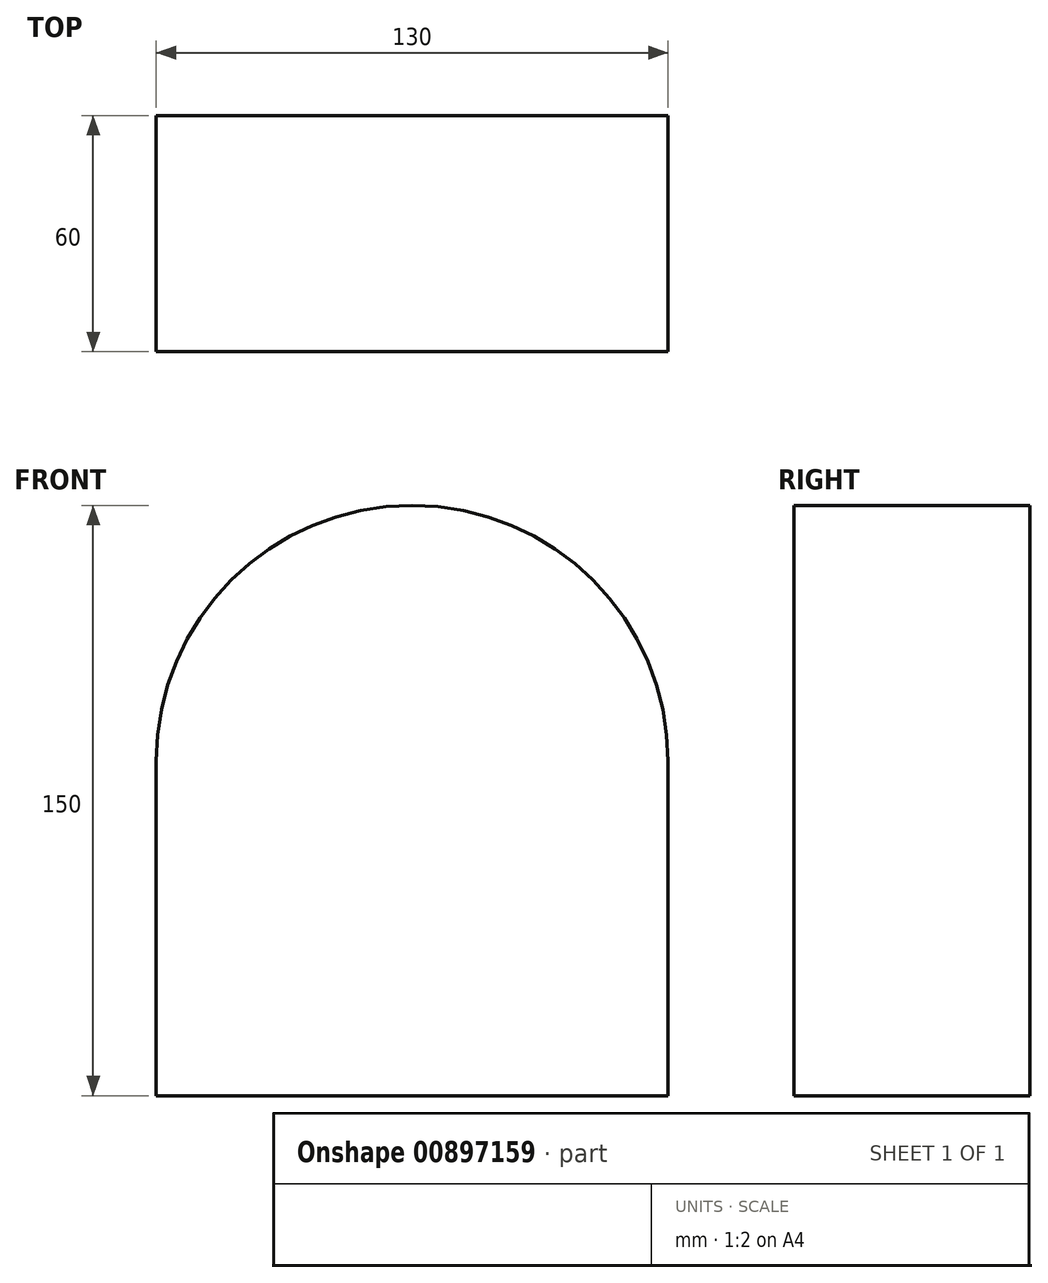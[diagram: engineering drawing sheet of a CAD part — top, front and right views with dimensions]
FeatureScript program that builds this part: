
annotation { "Feature Type Name" : "Feature", "Feature Type Description" : "" }
export const myFeature = defineFeature(function(context is Context, id is Id, definition is map)
    precondition{}
    {
        {
            var Q0;
            Q0=qCreatedBy(makeId("Front.planeOp"),FACE);
            var sketch = newSketch(context, id + "F0", { "sketchPlane" : qUnion([Q0])});
            skLineSegment(sketch, "E0.bottom", {"start": v(-65, 0) * mm, "end": v(65, 0) * mm});
            skLineSegment(sketch, "E0.top", {"start": v(0, 150) * mm, "end": v(0, 150) * mm});
            skLineSegment(sketch, "E0.left", {"start": v(-65, 0) * mm, "end": v(-65, 85) * mm});
            skLineSegment(sketch, "E0.right", {"start": v(65, 0) * mm, "end": v(65, 85) * mm});
            skLineSegment(sketch, "E1", {"start": v(0, 150) * mm, "end": v(0, 0) * mm, "construction": true});
            skPoint(sketch, "E2.visualSharp", {"position": v(-65, 150) * mm});
            skArc(sketch, "E2.filletArc", {"start": v(0, 150) * mm, "mid": v(-45.96, 130.96) * mm, "end": v(-65, 85) * mm});
            skPoint(sketch, "E3.visualSharp", {"position": v(65, 150) * mm});
            skArc(sketch, "E3.filletArc", {"start": v(65, 85) * mm, "mid": v(45.96, 130.96) * mm, "end": v(0, 150) * mm});
            skPoint(sketch, "E4.visualSharp", {"position": v(-65, 0) * mm});
            skPoint(sketch, "E5.visualSharp", {"position": v(65, 0) * mm});
            skSolve(sketch);
        }
        {
            var Q0;
            Q0=qCreatedBy(makeId("Top.planeOp"),FACE);
            var sketch = newSketch(context, id + "F1", { "sketchPlane" : qUnion([Q0])});
            skLineSegment(sketch, "E6.bottom", {"start": v(27.5, -46) * mm, "end": v(-27.5, -46) * mm});
            skLineSegment(sketch, "E6.top", {"start": v(27.5, 46) * mm, "end": v(-27.5, 46) * mm});
            skLineSegment(sketch, "E6.left", {"start": v(27.5, -46) * mm, "end": v(27.5, 46) * mm});
            skLineSegment(sketch, "E6.right", {"start": v(-27.5, -46) * mm, "end": v(-27.5, 46) * mm});
            skPoint(sketch, "E6.middle", {"position": v(0, 0) * mm});
            skSolve(sketch);
        }
        {
            var Q0;
            Q0=qCreatedBy(makeId("Front.planeOp"),FACE);
            var sketch = newSketch(context, id + "F2", { "sketchPlane" : qUnion([Q0])});
            skLineSegment(sketch, "E7.bottom", {"start": v(-43.5, 98.93) * mm, "end": v(43.5, 98.93) * mm});
            skLineSegment(sketch, "E7.top", {"start": v(-43.5, 36.93) * mm, "end": v(43.5, 36.93) * mm});
            skLineSegment(sketch, "E7.left", {"start": v(-43.5, 98.93) * mm, "end": v(-43.5, 36.93) * mm});
            skLineSegment(sketch, "E7.right", {"start": v(43.5, 98.93) * mm, "end": v(43.5, 36.93) * mm});
            skCircle(sketch, "E8", {"center": v(0, 67.93) * mm, "radius": 60 * mm});
            skLineSegment(sketch, "E9", {"start": v(-43.5, 67.93) * mm, "end": v(-60, 67.93) * mm});
            skLineSegment(sketch, "E10", {"start": v(43.5, 67.93) * mm, "end": v(60, 67.93) * mm});
            skLineSegment(sketch, "E11", {"start": v(0, 98.93) * mm, "end": v(0, 36.93) * mm});
            skLineSegment(sketch, "E12.bottom", {"start": v(-65, 0) * mm, "end": v(65, 0) * mm});
            skLineSegment(sketch, "E12.top", {"start": v(-65, -12.86) * mm, "end": v(65, -12.86) * mm});
            skLineSegment(sketch, "E12.left", {"start": v(-65, 0) * mm, "end": v(-65, -12.86) * mm});
            skLineSegment(sketch, "E12.right", {"start": v(65, 0) * mm, "end": v(65, -12.86) * mm});
            skSolve(sketch);
        }
        {
            var Q0;
            Q0 = qSketchRegion(id + "F0", true);
            extrude(context, id + "F3", {"entities" : qUnion([Q0]), "depth" : 60 * mm, "offsetDistance" : 25 * mm});
        }
        {
            var Q0;
            Q0=qCreatedBy(makeId("Top.planeOp"),FACE);
            var Q1;
            Q1=makeQuery(id+"F3.opExtrude","CAP_VERTEX",VERTEX,{"disambiguationData":[OSD([sQuery(id+"F0.wireOp",EDGE,"E0.left"),sQuery(id+"F0.wireOp",EDGE,"E2.filletArc")])],"isStart":true});
            cPlane(context, id + "F4", {"entities" : qUnion([Q0, Q1]), "cplaneType" : CPlaneType.PLANE_POINT, "offset" : 25 * mm, "width" : 150 * mm, "height" : 150 * mm});
        }
    });
